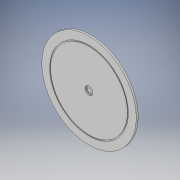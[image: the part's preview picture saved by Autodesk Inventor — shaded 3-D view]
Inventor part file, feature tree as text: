
AUTODESK INVENTOR PART (.ipt)
format: ipt  version: 2019 (Build 230136000, 136)  size: 125,952 bytes
history: native  units: in
note: dims shown in document units (in); Inventor stores cm internally (conversion verified against a paired STEP export)
features: sketch x4, extrude x3
ambient origin geometry x8: Origin, YZ Plane, XZ Plane, XY Plane, X Axis, Y Axis, Z Axis, Center Point
bodies: Solid1 (feature_tree)
feature tree (7):
  extrude  "Extrusion1"  Depth=1.0in
  sketch  "Sketch2"  dims[d2=0.25in d3=0.0in d4=10.0in]
  extrude  "Extrusion2"  Depth=0.25in
  extrude  "Extrusion3"  Depth=0.05in TaperAngle=0.0deg
  sketch  "Sketch1"  dims[d0=12.0in d1=1.0in]
  sketch  "Sketch3"  dims[d5=9.75in d6=0.05in d7=0.0in]
  sketch  "Sketch4"  dims[d8=10.0in d9=9.75in d10=0.05in d11=0.0in]
